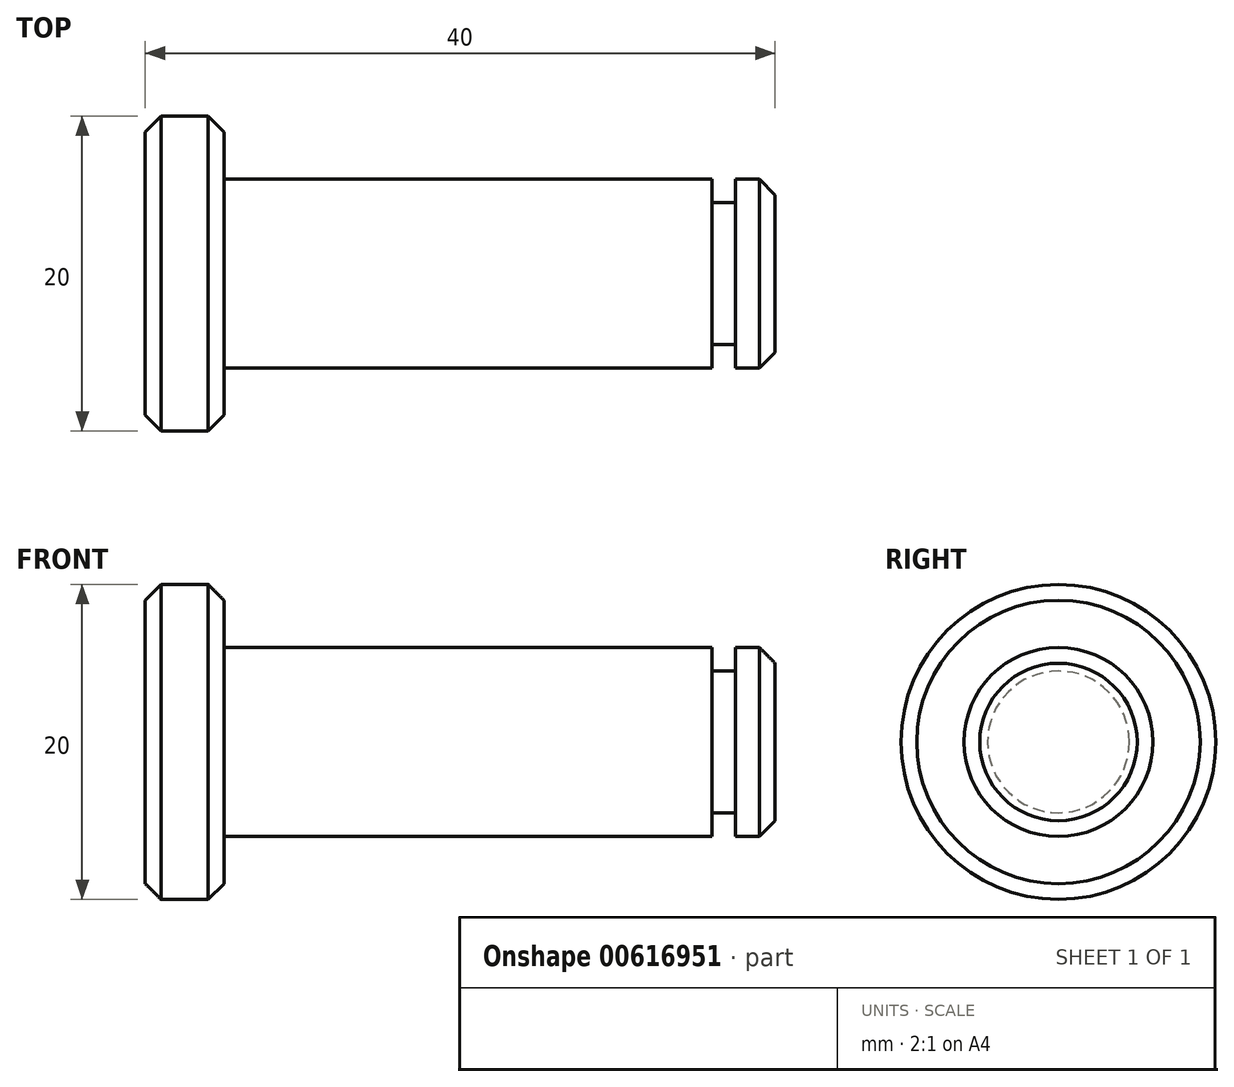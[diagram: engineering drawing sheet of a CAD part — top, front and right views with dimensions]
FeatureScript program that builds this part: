
annotation { "Feature Type Name" : "Feature", "Feature Type Description" : "" }
export const myFeature = defineFeature(function(context is Context, id is Id, definition is map)
    precondition{}
    {
        {
            var Q0;
            Q0=qCreatedBy(makeId("Front.planeOp"),FACE);
            var sketch = newSketch(context, id + "F0", { "sketchPlane" : qUnion([Q0])});
            skLineSegment(sketch, "E0", {"start": v(-40.03, 0) * mm, "end": v(-40.03, 10) * mm});
            skLineSegment(sketch, "E1", {"start": v(-40.03, 10) * mm, "end": v(-35.03, 10) * mm});
            skLineSegment(sketch, "E2", {"start": v(-35.03, 10) * mm, "end": v(-35.03, 6) * mm});
            skLineSegment(sketch, "E3", {"start": v(-35.03, 6) * mm, "end": v(-4.03, 6) * mm});
            skLineSegment(sketch, "E4", {"start": v(-4.03, 6) * mm, "end": v(-4.03, 4.5) * mm});
            skLineSegment(sketch, "E5", {"start": v(-4.03, 4.5) * mm, "end": v(-2.53, 4.5) * mm});
            skLineSegment(sketch, "E6", {"start": v(-2.53, 4.5) * mm, "end": v(-2.53, 6) * mm});
            skLineSegment(sketch, "E7", {"start": v(-2.53, 6) * mm, "end": v(-0.03, 6) * mm});
            skLineSegment(sketch, "E8", {"start": v(-0.03, 6) * mm, "end": v(-0.03, 0) * mm});
            skLineSegment(sketch, "E9", {"start": v(-0.03, 0) * mm, "end": v(-40.03, 0) * mm});
            skSolve(sketch);
        }
        {
            var Q0;
            Q0 = qSketchRegion(id + "F0", true);
            var Q1;
            Q1=sQuery(id+"F0.wireOp",EDGE,"E9");
            revolve(context, id + "F1", {"entities" : qUnion([Q0]), "axis" : qUnion([Q1]), "revolveType" : RevolveType.FULL});
        }
        {
            var Q0;
            Q0=makeQuery(id+"F1.opRevolve","SWEPT_EDGE",EDGE,{"disambiguationData":[OSD([sQuery(id+"F0.wireOp",EDGE,"E1"),sQuery(id+"F0.wireOp",EDGE,"E2")])]});
            var Q1;
            Q1=makeQuery(id+"F1.opRevolve","SWEPT_EDGE",EDGE,{"disambiguationData":[OSD([sQuery(id+"F0.wireOp",EDGE,"E7"),sQuery(id+"F0.wireOp",EDGE,"E8")])]});
            var Q2;
            Q2=makeQuery(id+"F1.opRevolve","SWEPT_EDGE",EDGE,{"disambiguationData":[OSD([sQuery(id+"F0.wireOp",EDGE,"E0"),sQuery(id+"F0.wireOp",EDGE,"E1")])]});
            chamfer(context, id + "F2", {"entities" : qUnion([Q0, Q1, Q2]), "width" : 1 * mm, "tangentPropagation" : true});
        }
    });
